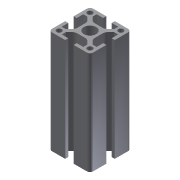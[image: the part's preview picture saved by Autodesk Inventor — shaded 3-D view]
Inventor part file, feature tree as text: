
AUTODESK INVENTOR PART (.ipt)
format: ipt  version: 2014 (Build 180170000, 170)  size: 190,464 bytes
history: native  units: mm
features: other x42, sketch x5, hole x4, extrude x1
ambient origin geometry x8: Origin, YZ Plane, XZ Plane, XY Plane, X Axis, Y Axis, Z Axis, Center Point
bodies: Solid1 (feature_tree)
feature tree (52):
  extrude  "Extrusion1"  [1 undecoded]
  hole  "Drilling 1"  [1 undecoded]
  hole  "Drilling 2"  [1 undecoded]
  hole  "Drilling 3"  [1 undecoded]
  hole  "Drilling 4"  [1 undecoded]
  other  "side_4d_XY"
  other  "side_4d_YZ"
  other  "side_4d_ZX"
  other  "side_4d_X"
  other  "side_4d_Y"
  other  "side_4d_Z"
  other  "side_4d_Center"
  other  "side_1a_XY"
  other  "side_1a_YZ"
  other  "side_1a_ZX"
  other  "side_1a_X"
  other  "side_1a_Y"
  other  "side_1a_Z"
  other  "side_1a_Center"
  other  "side_2b_XY"
  other  "side_2b_YZ"
  other  "side_2b_ZX"
  other  "side_2b_X"
  other  "side_2b_Y"
  other  "side_2b_Z"
  other  "side_2b_Center"
  other  "side_3c_XY"
  other  "side_3c_YZ"
  other  "side_3c_ZX"
  other  "side_3c_X"
  other  "side_3c_Y"
  other  "side_3c_Z"
  other  "side_3c_Center"
  other  "end_XY"
  other  "end_YZ"
  other  "end_ZX"
  other  "end_X"
  other  "end_Y"
  other  "end_Z"
  other  "end_Center"
  other  "start_XY"
  other  "start_YZ"
  other  "start_ZX"
  other  "start_X"
  other  "start_Y"
  other  "start_Z"
  other  "start_Center"
  sketch  "Skizze_1"  dims[d0=100.0mm d1=0.0mm]
  sketch  "Sketch2"  dims[d2=5.0mm d3=6.0mm d4=4.0mm d5=2.0mm d6=90.0deg d7=6000.0mm d8=0.0mm]
  sketch  "Sketch3"  dims[d9=5.0mm d10=6.0mm d11=4.0mm d12=2.0mm d13=90.0deg d14=6000.0mm d15=0.0mm]
  sketch  "Sketch4"  dims[d16=5.0mm d17=6.0mm d18=4.0mm d19=2.0mm d20=90.0deg d21=6000.0mm d22=0.0mm]
  sketch  "Sketch5"  dims[d23=5.0mm d24=6.0mm d25=4.0mm d26=2.0mm d27=90.0deg d28=6000.0mm d29=0.0mm]
note: 5 required parameter values undecoded (feature->parameter linkage not recoverable at this tier; creation-order binding heuristic only, values carry confidence <= 0.55)
